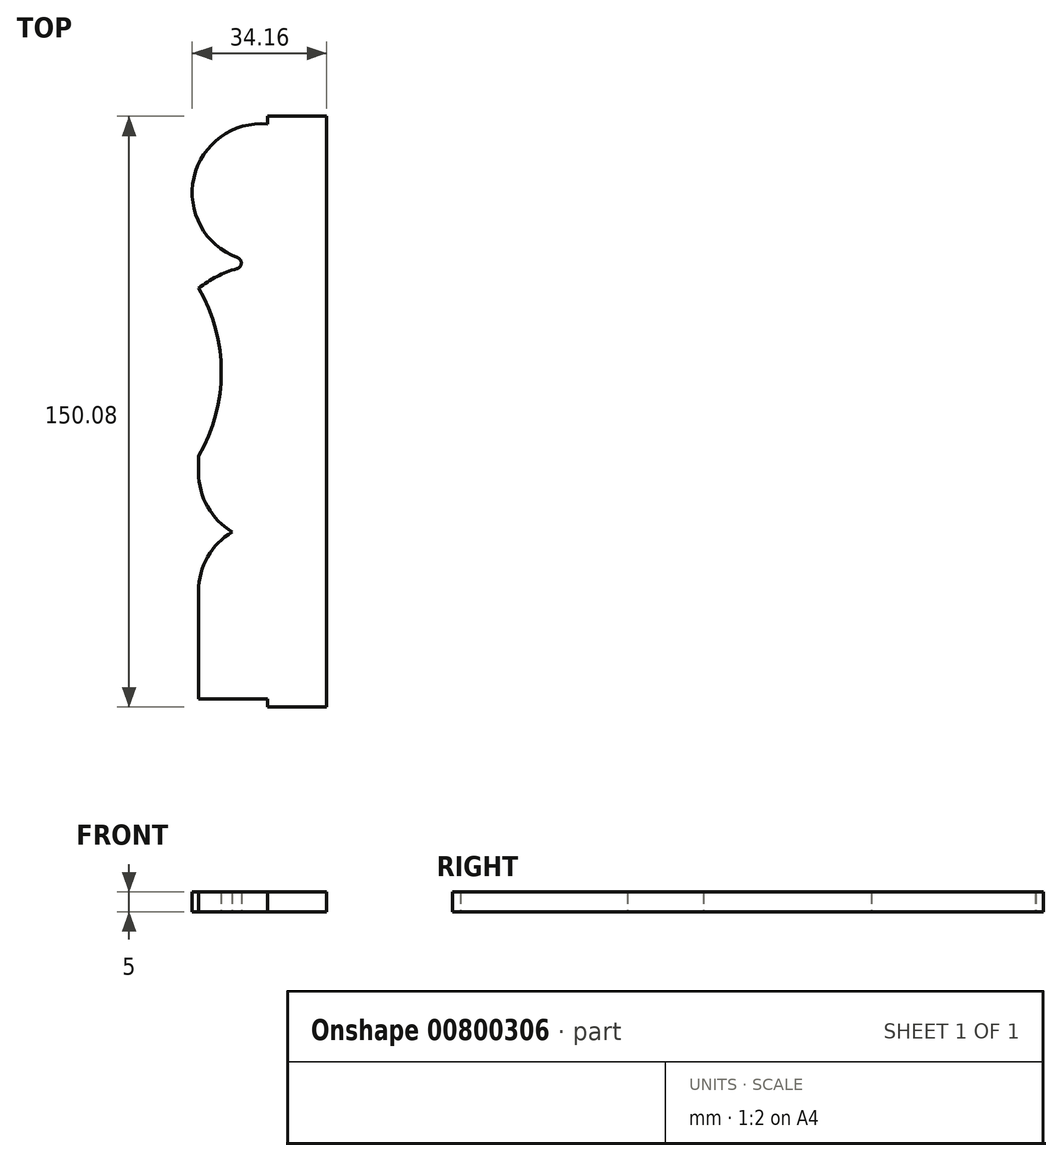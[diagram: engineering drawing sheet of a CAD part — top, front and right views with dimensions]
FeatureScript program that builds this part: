
annotation { "Feature Type Name" : "Feature", "Feature Type Description" : "" }
export const myFeature = defineFeature(function(context is Context, id is Id, definition is map)
    precondition{}
    {
        {
            var Q0;
            Q0=qCreatedBy(makeId("Top.planeOp"),FACE);
            var sketch = newSketch(context, id + "F0", { "sketchPlane" : qUnion([Q0])});
            skLineSegment(sketch, "E0", {"start": v(0, 0) * mm, "end": v(0, 150) * mm});
            skLineSegment(sketch, "E1", {"start": v(-17.5, 128.65) * mm, "end": v(-17.5, 121.21) * mm});
            skLineSegment(sketch, "E2", {"start": v(-1.66, 128.65) * mm, "end": v(0, 128.65) * mm});
            skArc(sketch, "E3", {"start": v(-17.5, 61.8) * mm, "mid": v(-11.76, 83.1) * mm, "end": v(-17.5, 104.4) * mm});
            skArc(sketch, "E4", {"start": v(-7.76, 109.35) * mm, "mid": v(-6.66, 110.74) * mm, "end": v(-7.65, 112.21) * mm});
            skArc(sketch, "E5.trimOffspring", {"start": v(-7.76, 109.35) * mm, "mid": v(-12.88, 107.36) * mm, "end": v(-17.5, 104.4) * mm});
            skArc(sketch, "E6.trimOffspring", {"start": v(0, 146.08) * mm, "mid": v(-18.73, 132.51) * mm, "end": v(-7.65, 112.21) * mm});
            skPoint(sketch, "E7.start.orphan", {"position": v(0, 131.43) * mm});
            skArc(sketch, "E8", {"start": v(-9, 42.5) * mm, "mid": v(-15.23, 36.1) * mm, "end": v(-17.5, 27.48) * mm});
            skLineSegment(sketch, "E9.trimOffspring", {"start": v(-17.5, 61.8) * mm, "end": v(-17.5, 57.5) * mm});
            skLineSegment(sketch, "E10.trimOffspring", {"start": v(-17.5, 27.48) * mm, "end": v(-17.5, 0) * mm});
            skArc(sketch, "E11.trimOffspring", {"start": v(-15.82, 64.98) * mm, "mid": v(-16.75, 52.42) * mm, "end": v(-9, 42.5) * mm});
            skPoint(sketch, "E12.orphan", {"position": v(17.5, 128.65) * mm});
            skPoint(sketch, "E13.end.orphan", {"position": v(17.5, 0) * mm});
            skLineSegment(sketch, "E14", {"start": v(-17.5, 0) * mm, "end": v(0, 0) * mm});
            skLineSegment(sketch, "E15", {"start": v(0, 146.08) * mm, "end": v(0, 148.08) * mm});
            skLineSegment(sketch, "E16", {"start": v(0, 148.08) * mm, "end": v(15, 148.08) * mm});
            skLineSegment(sketch, "E17", {"start": v(15, 148.08) * mm, "end": v(15, -2) * mm});
            skLineSegment(sketch, "E18", {"start": v(15, -2) * mm, "end": v(0, -2) * mm});
            skLineSegment(sketch, "E19", {"start": v(0, -2) * mm, "end": v(0, 0) * mm});
            skSolve(sketch);
        }
        {
            var Q0;
            Q0 = qSketchRegion(id + "F0", true);
            extrude(context, id + "F1", {"entities" : qUnion([Q0]), "depth" : 5 * mm, "offsetDistance" : 25 * mm});
        }
    });
